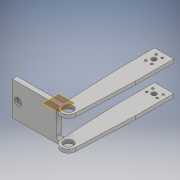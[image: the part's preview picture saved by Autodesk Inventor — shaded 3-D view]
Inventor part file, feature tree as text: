
AUTODESK INVENTOR PART (.ipt)
format: ipt  version: 2017 (Build 210142000, 142)  size: 262,144 bytes
history: native  units: in
note: dims shown in document units (in); Inventor stores cm internally (conversion verified against a paired STEP export)
features: sketch x9, projected_geometry x9, hole x5, extrude x4, plane x2, fillet x2
ambient origin geometry x8: Origin, YZ Plane, XZ Plane, XY Plane, X Axis, Y Axis, Z Axis, Center Point
bodies: Solid1 (feature_tree)
feature tree (31):
  sketch  "Sketch1"  dims[d0=5.0in d1=1.0in]
  plane  "Work Plane1"
  extrude  "Extrusion2"  Depth=1.0in
  plane  "Work Plane2"
  extrude  "Extrusion3"  Depth=1.0in
  hole  "Hole2"  [1 undecoded]
  extrude  "Extrusion4"  Depth=1.753in
  extrude  "Extrusion5"  Depth=1.753in
  fillet  "Fillet1"  Radius=2.0in
  fillet  "Fillet2"  Radius=1.753in
  hole  "Hole3"  [1 undecoded]
  hole  "Hole4"  [1 undecoded]
  hole  "Hole5"  [1 undecoded]
  hole  "Hole6"  [1 undecoded]
  sketch  "Sketch2"  dims[d5=1.0in d6=0.75in]
  projected_geometry  "Projected Loop1"
  sketch  "Sketch4"  dims[d7=0.5in d8=0.0in]
  projected_geometry  "Projected Loop3"
  sketch  "Sketch5"  dims[d9=1.753in d10=0.0in d18=0.75in]
  projected_geometry  "Projected Loop4"
  sketch  "Sketch8"  dims[d19=0.125in d20=2.0in d21=2.0in d22=1.753in d23=0.0in]
  projected_geometry  "Projected Loop9"
  projected_geometry  "Projected Loop10"
  sketch  "Sketch9"  dims[d24=0.505in d25=0.75in d26=0.375in d27=0.25in d28=0.5635in d29=1.0in d30=0.8108in d31=2.5in]
  projected_geometry  "Projected Loop11"
  sketch  "Sketch10"  dims[d32=0.25in d33=0.375in]
  projected_geometry  "Projected Loop12"
  sketch  "Sketch11"  dims[d34=0.3125in d35=5.0in]
  projected_geometry  "Projected Loop13"
  sketch  "Sketch12"  dims[d36=4.875in d37=1.753in d38=0.0in d41=1.753in d42=5.375in d43=1.378in d44=0.1875in d45=5.875in d46=1.0in d47=0.0in d48=0.125in d49=0.125in d50=0.6299in d51=1.0in d52=0.5in d53=0.315in d54=0.1575in d55=0.117in d56=0.75in d57=0.375in d58=0.25in d59=0.5635in d60=1.0in d61=0.8108in d62=0.6299in d63=1.0in d64=0.5in d65=0.315in d66=0.1575in d67=0.117in d68=0.75in d69=0.375in d70=0.25in d71=0.5635in d72=1.0in d73=0.8108in d74=0.3125in d75=1.753in d76=0.8765in d77=0.375in d78=0.75in d79=0.375in d80=0.25in d81=0.5635in d82=0.125in d83=0.8108in d84=1.0in d85=0.5in d86=0.5455in d87=0.2728in d88=0.25in d89=0.75in d90=0.375in d91=0.25in d92=0.5635in d93=1.0in d94=0.8108in]
  projected_geometry  "Projected Loop14"
note: 5 required parameter values undecoded (feature->parameter linkage not recoverable at this tier; creation-order binding heuristic only, values carry confidence <= 0.55)
